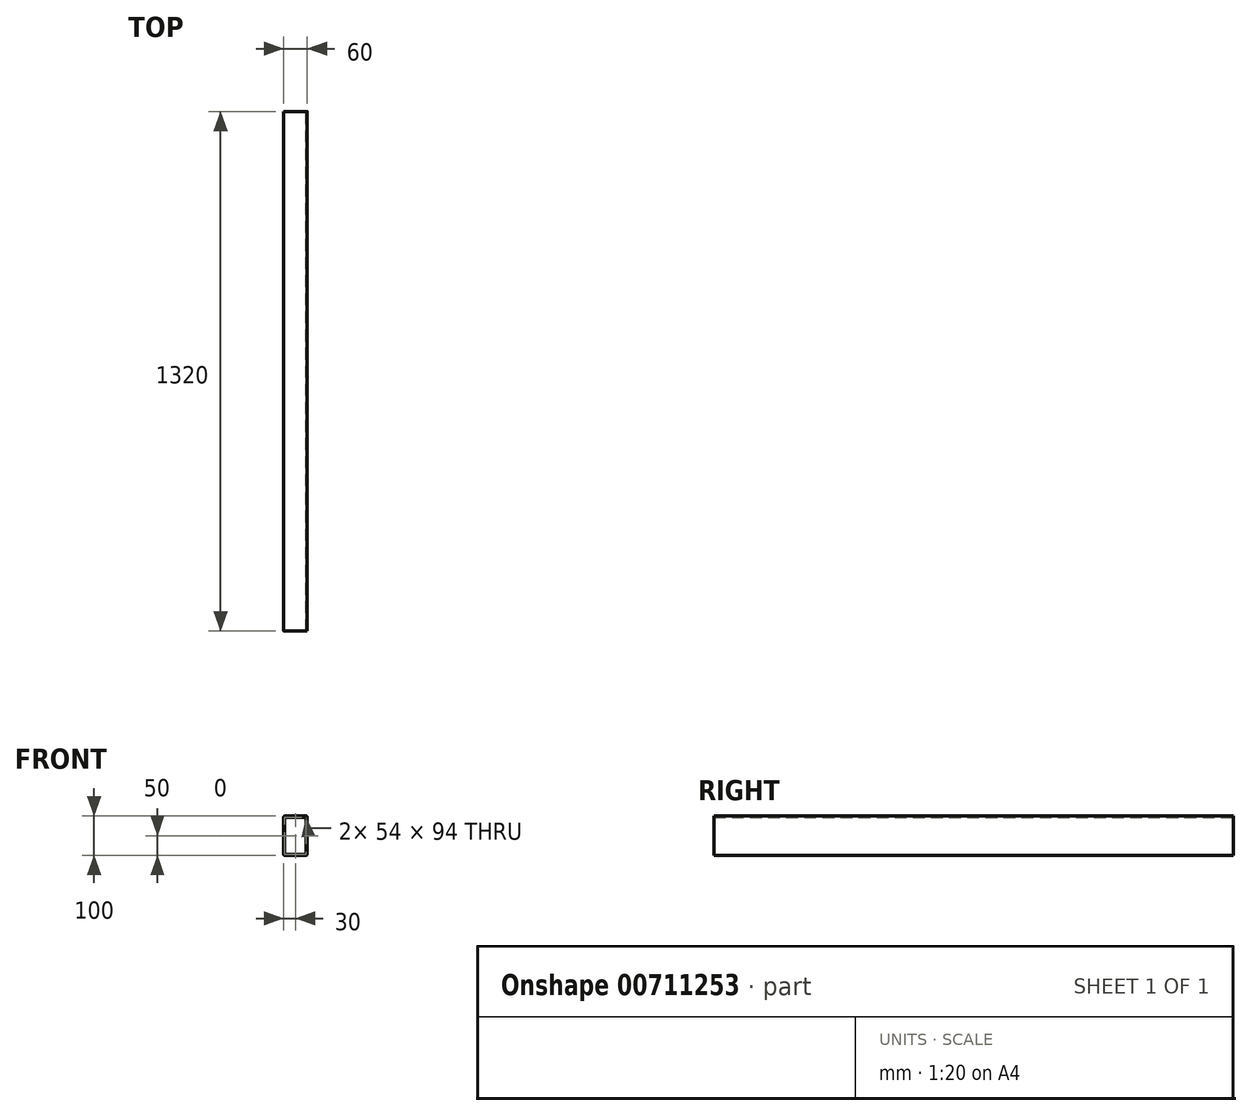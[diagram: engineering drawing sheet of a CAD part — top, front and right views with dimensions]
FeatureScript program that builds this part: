
annotation { "Feature Type Name" : "Feature", "Feature Type Description" : "" }
export const myFeature = defineFeature(function(context is Context, id is Id, definition is map)
    precondition{}
    {
        {
            var Q0;
            Q0=qCreatedBy(makeId("Front.planeOp"),FACE);
            var sketch = newSketch(context, id + "F0", { "sketchPlane" : qUnion([Q0])});
            skLineSegment(sketch, "E0.bottom", {"start": v(27, 50) * mm, "end": v(-27, 50) * mm});
            skLineSegment(sketch, "E0.top", {"start": v(27, -50) * mm, "end": v(-27, -50) * mm});
            skLineSegment(sketch, "E0.left", {"start": v(30, 47) * mm, "end": v(30, -47) * mm});
            skLineSegment(sketch, "E0.right", {"start": v(-30, 47) * mm, "end": v(-30, -47) * mm});
            skPoint(sketch, "E0.middle", {"position": v(0, 0) * mm});
            skPoint(sketch, "E1.visualSharp", {"position": v(-30, 50) * mm});
            skArc(sketch, "E1.filletArc", {"start": v(-27, 50) * mm, "mid": v(-29.12, 49.12) * mm, "end": v(-30, 47) * mm});
            skPoint(sketch, "E2.visualSharp", {"position": v(30, 50) * mm});
            skArc(sketch, "E2.filletArc", {"start": v(30, 47) * mm, "mid": v(29.12, 49.12) * mm, "end": v(27, 50) * mm});
            skPoint(sketch, "E3.visualSharp", {"position": v(30, -50) * mm});
            skArc(sketch, "E3.filletArc", {"start": v(27, -50) * mm, "mid": v(29.12, -49.12) * mm, "end": v(30, -47) * mm});
            skPoint(sketch, "E4.visualSharp", {"position": v(-30, -50) * mm});
            skArc(sketch, "E4.filletArc", {"start": v(-30, -47) * mm, "mid": v(-29.12, -49.12) * mm, "end": v(-27, -50) * mm});
            skLineSegment(sketch, "E5.bottom", {"start": v(27, 47) * mm, "end": v(-27, 47) * mm});
            skLineSegment(sketch, "E5.top", {"start": v(27, -47) * mm, "end": v(-27, -47) * mm});
            skLineSegment(sketch, "E5.left", {"start": v(27, 47) * mm, "end": v(27, -47) * mm});
            skLineSegment(sketch, "E5.right", {"start": v(-27, 47) * mm, "end": v(-27, -47) * mm});
            skSolve(sketch);
        }
        {
            var Q0;
            Q0=makeQuery(id+"F0.imprint","IMPRINT",FACE,{"disambiguationData":[TD([[makeQuery(id+"F0.imprint","IMPRINT",EDGE,{"derivedFrom":sQuery(id+"F0.wireOp",EDGE,"E0.bottom")}),1.0]])]});
            extrude(context, id + "F1", {"entities" : qUnion([Q0]), "depth" : 1320 * mm, "offsetDistance" : 25 * mm});
        }
    });
